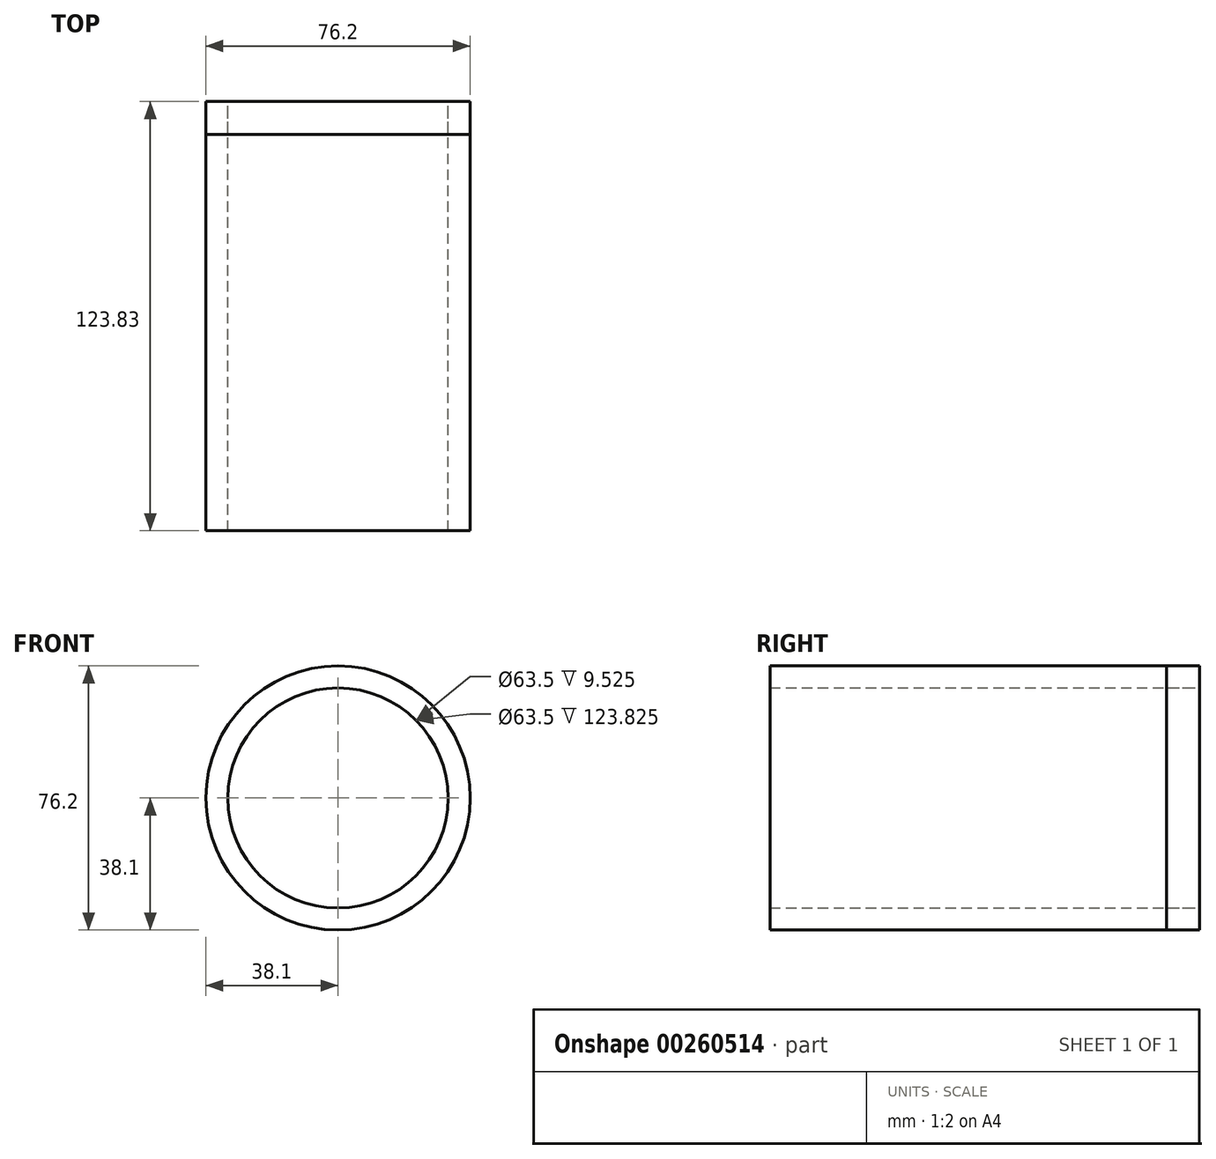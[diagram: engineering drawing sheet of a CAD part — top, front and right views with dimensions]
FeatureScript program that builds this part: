
annotation { "Feature Type Name" : "Feature", "Feature Type Description" : "" }
export const myFeature = defineFeature(function(context is Context, id is Id, definition is map)
    precondition{}
    {
        {
            var Q0;
            Q0=qCreatedBy(makeId("Front.planeOp"),FACE);
            var sketch = newSketch(context, id + "F0", { "sketchPlane" : qUnion([Q0])});
            skCircle(sketch, "E0", {"center": v(0, 0) * mm, "radius": 38.1 * mm});
            skCircle(sketch, "E1", {"center": v(0, 0) * mm, "radius": 31.75 * mm});
            skSolve(sketch);
        }
        {
            var Q0;
            Q0 = qSketchRegion(id + "F0", true);
            extrude(context, id + "F1", {"entities" : qUnion([Q0]), "depth" : 123.82 * mm});
        }
        {
            var Q0;
            Q0 = qSketchRegion(id + "F0", true);
            extrude(context, id + "F2", {"entities" : qUnion([Q0]), "depth" : 9.52 * mm});
        }
    });
